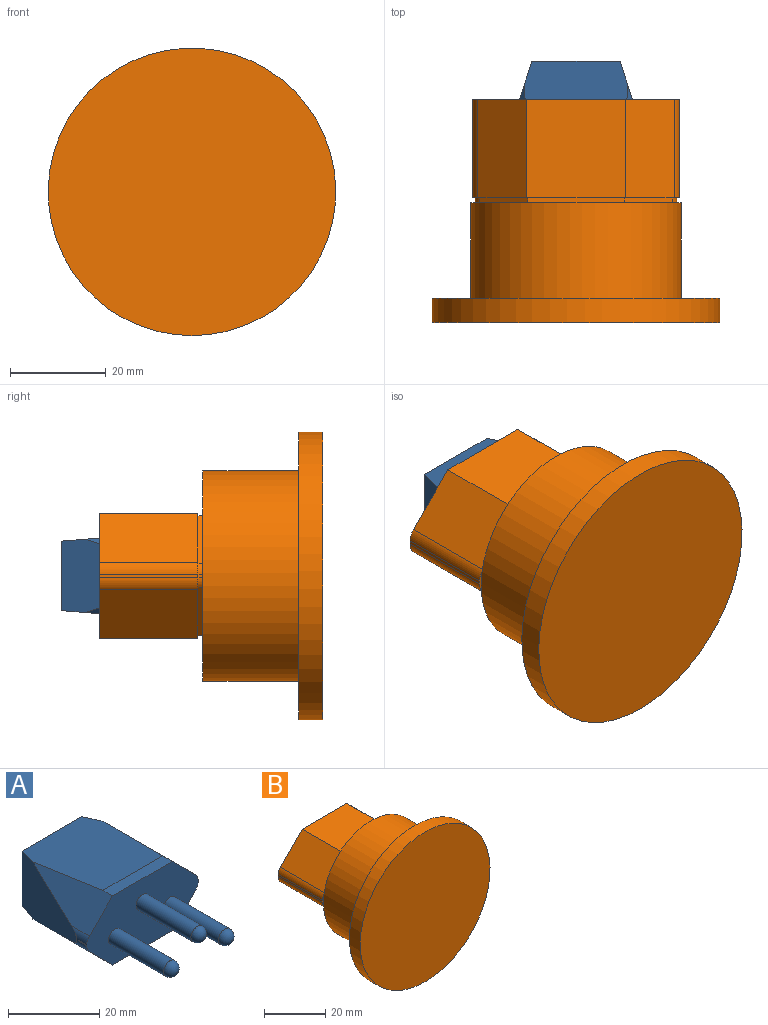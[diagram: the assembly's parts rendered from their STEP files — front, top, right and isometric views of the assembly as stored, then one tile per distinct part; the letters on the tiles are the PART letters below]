
ASSEMBLY  parts=2 mates=1
PART A: 24 faces, bbox 34.5x47x18.5 mm
  f0: plane 18.5x3mm, normal (0,0,-1), area 55.5mm2, adj f5,f9,f10,f15
  f1: plane 3x0.18mm, normal (1,0,0), area 0.5mm2, adj f5,f14,f20,f22
  f2: plane 18.5x3mm, normal (0,0,1), area 55.5mm2, adj f5,f11,f12,f16
  f3: plane 3x0.18mm, normal (-1,0,0), area 0.5mm2, adj f5,f13,f21,f23
  f4: plane 18.5x14.5mm, normal (0,1,0), area 268.2mm2, adj f13,f14,f15,f16
  f5: plane 34.5x18.5mm, normal (0,-1,0), area 471.9mm2, adj f0,f1,f2,f3,f6,f7,f8,f9
  f6: cylinder r=2mm len=17mm, axis (0,1,0), area 213.6mm2, adj f5,f19
  f7: cylinder r=2mm len=17mm, axis (0,1,0), area 213.6mm2, adj f5,f18
  f8: cylinder r=2mm len=17mm, axis (0,1,0), area 213.6mm2, adj f5,f17
  f9: plane 23x7.18mm, normal (-0.71,0,-0.71), area 142.1mm2, adj f0,f5,f13,f15,f21
  f10: plane 23x7.18mm, normal (0.71,0,-0.71), area 142.1mm2, adj f0,f5,f14,f15,f22
  f11: plane 23x7.18mm, normal (-0.71,0,0.71), area 142.1mm2, adj f2,f5,f13,f16,f23
  f12: plane 23x7.18mm, normal (0.71,0,0.71), area 142.1mm2, adj f2,f5,f14,f16,f20
  f13: plane 25x15.3mm, normal (-0.95,0.3,0), area 264mm2, adj f3,f4,f9,f11,f15,f16,f21,f23
  f14: plane 25x15.3mm, normal (0.95,0.3,0), area 264mm2, adj f1,f4,f10,f12,f15,f16,f20,f22
  f15: plane 25x21.7mm, normal (0,0.08,-1), area 504.1mm2, adj f0,f4,f9,f10,f13,f14
  f16: plane 25x21.7mm, normal (0,0.08,1), area 504.1mm2, adj f2,f4,f11,f12,f13,f14
  f17: sphere r=2mm, area 25.1mm2, adj f8
  f18: sphere r=2mm, area 25.1mm2, adj f7
  f19: sphere r=2mm, area 25.1mm2, adj f6
  f20: cylinder r=2.8mm len=5.56mm, axis (0,1,0), area 8.5mm2, adj f1,f5,f12,f14
  f21: cylinder r=2.8mm len=5.56mm, axis (0,-1,0), area 8.5mm2, adj f3,f5,f9,f13
  f22: cylinder r=2.8mm len=5.56mm, axis (0,1,0), area 8.5mm2, adj f1,f5,f10,f14
  f23: cylinder r=2.8mm len=5.56mm, axis (0,-1,0), area 8.5mm2, adj f3,f5,f11,f13
PART B: 50 faces, bbox 60x46.5x60 mm
  f0: cylinder r=2.25mm len=20mm, axis (0,1,0), area 282.7mm2, adj f28,f47
  f1: cylinder r=2.25mm len=20mm, axis (0,1,0), area 282.7mm2, adj f28,f48
  f2: cylinder r=2.25mm len=20mm, axis (0,1,0), area 282.7mm2, adj f28,f49
  f3: plane 43x26mm, normal (0,1,0), area 209.5mm2, adj f4,f5,f6,f7,f8,f9,f10,f11
  f4: plane 20.66x20.5mm, normal (0,0,-1), area 423.5mm2, adj f3,f5,f15,f41
  f5: plane 20.5x10.15mm, normal (0.71,0,-0.71), area 294.2mm2, adj f3,f4,f6,f41
  f6: cylinder r=3.5mm len=20.5mm, axis (0,-1,0), area 56.4mm2, adj f3,f5,f7,f41
  f7: plane 20.5x0.76mm, normal (1,0,0), area 15.5mm2, adj f3,f6,f8,f41
  f8: cylinder r=3.5mm len=20.5mm, axis (0,-1,0), area 56.4mm2, adj f3,f7,f9,f41
  f9: plane 20.5x10.15mm, normal (0.71,0,0.71), area 294.2mm2, adj f3,f8,f10,f41
  f10: plane 20.66x20.5mm, normal (0,0,1), area 423.5mm2, adj f3,f9,f11,f41
  f11: plane 20.5x10.15mm, normal (-0.71,0,0.71), area 294.2mm2, adj f3,f10,f12,f41
  f12: cylinder r=3.5mm len=20.5mm, axis (0,-1,0), area 56.4mm2, adj f3,f11,f13,f41
  f13: plane 20.5x0.76mm, normal (-1,0,0), area 15.5mm2, adj f3,f12,f14,f41
  f14: cylinder r=3.5mm len=20.5mm, axis (0,-1,0), area 56.4mm2, adj f3,f13,f15,f41
  f15: plane 20.5x10.15mm, normal (-0.71,0,-0.71), area 294.2mm2, adj f3,f4,f14,f41
  f16: plane 20x19mm, normal (0,0,1), area 380mm2, adj f3,f17,f27,f28
  f17: plane 20x9.56mm, normal (-0.71,0,0.71), area 270.4mm2, adj f3,f16,f18,f28
  f18: cylinder r=1.5mm len=20mm, axis (0,-1,0), area 23.6mm2, adj f3,f17,f19,f28
  f19: plane 20x0.76mm, normal (-1,0,0), area 15.1mm2, adj f3,f18,f20,f28
  f20: cylinder r=1.5mm len=20mm, axis (0,-1,0), area 23.6mm2, adj f3,f19,f21,f28
  f21: plane 20x9.56mm, normal (-0.71,0,-0.71), area 270.4mm2, adj f3,f20,f22,f28
  f22: plane 20x19mm, normal (0,0,-1), area 380mm2, adj f3,f21,f23,f28
  f23: plane 20x9.56mm, normal (0.71,0,-0.71), area 270.4mm2, adj f3,f22,f24,f28
  f24: cylinder r=1.5mm len=20mm, axis (0,-1,0), area 23.6mm2, adj f3,f23,f25,f28
  f25: plane 20x0.76mm, normal (1,0,0), area 15.1mm2, adj f3,f24,f26,f28
  f26: cylinder r=1.5mm len=20mm, axis (0,-1,0), area 23.6mm2, adj f3,f25,f27,f28
  f27: plane 20x9.56mm, normal (0.71,0,0.71), area 270.4mm2, adj f3,f16,f26,f28
  f28: plane 39x22mm, normal (0,1,0), area 610.1mm2, adj f0,f1,f2,f16,f17,f18,f19,f20
  f29: cylinder r=3mm len=2.12mm, axis (0,-1,0), area 2.4mm2, adj f30,f40,f41,f42
  f30: plane 1x0.76mm, normal (-1,0,0), area 0.8mm2, adj f29,f31,f41,f42
  f31: cylinder r=3mm len=2.12mm, axis (0,-1,0), area 2.4mm2, adj f30,f32,f41,f42
  f32: plane 10x10mm, normal (-0.71,0,0.71), area 14.1mm2, adj f31,f33,f41,f42
  f33: plane 20.24x1mm, normal (0,0,1), area 20.2mm2, adj f32,f34,f41,f42
  f34: plane 10x10mm, normal (0.71,0,0.71), area 14.1mm2, adj f33,f35,f41,f42
  f35: cylinder r=3mm len=2.12mm, axis (0,-1,0), area 2.4mm2, adj f34,f36,f41,f42
  f36: plane 1x0.76mm, normal (1,0,0), area 0.8mm2, adj f35,f37,f41,f42
  f37: cylinder r=3mm len=2.12mm, axis (0,-1,0), area 2.4mm2, adj f36,f38,f41,f42
  f38: plane 10x10mm, normal (0.71,0,-0.71), area 14.1mm2, adj f37,f39,f41,f42
  f39: plane 20.24x1mm, normal (0,0,-1), area 20.2mm2, adj f38,f40,f41,f42
  f40: plane 10x10mm, normal (-0.71,0,-0.71), area 14.1mm2, adj f29,f39,f41,f42
  f41: plane 43x26mm, normal (0,-1,0), area 54.8mm2, adj f4,f5,f6,f7,f8,f9,f10,f11
  f42: plane 44x44mm, normal (0,1,0), area 708mm2, adj f29,f30,f31,f32,f33,f34,f35,f36
  f43: cylinder r=22mm len=44mm, axis (0,-1,0), area 2764.6mm2, adj f42,f46
  f44: plane 60x60mm, normal (0,-1,0), area 2827.4mm2, adj f45
  f45: cylinder r=30mm len=60mm, axis (0,1,0), area 942.5mm2, adj f44,f46
  f46: plane 60x60mm, normal (0,1,0), area 1306.9mm2, adj f43,f45
  f47: plane 4.5x4.5mm, normal (0,1,0), area 15.9mm2, adj f0
  f48: plane 4.5x4.5mm, normal (0,1,0), area 15.9mm2, adj f1
  f49: plane 4.5x4.5mm, normal (0,1,0), area 15.9mm2, adj f2
PLACE A rot(axis=(0.24,0.95,0.2),0deg) t=(1.15,-22.12,2.41)mm
PLACE B rot(axis=(0.73,-0.34,0.59),0deg) t=(1.15,-2.12,2.41)mm
MATE revolute A.f6 <-> B.f1  axis (0,-1,0) through (-7.35,-22.12,0.41)mm
